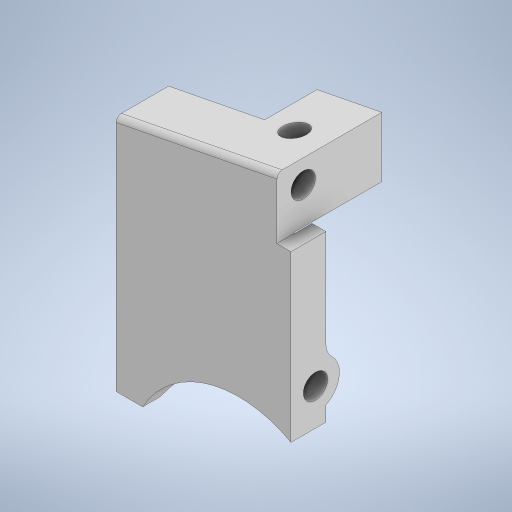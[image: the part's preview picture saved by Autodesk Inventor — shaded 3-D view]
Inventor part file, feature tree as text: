
AUTODESK INVENTOR PART (.ipt)
format: ipt  version: 2023.5 (Build 275446000, 446)  size: 538,112 bytes
history: native  units: mm
features: sketch x21, projected_geometry x19, extrude x17, reference x12, other x9, fillet x5, hole x4
ambient origin geometry x8: Origin, YZ Plane, XZ Plane, XY Plane, X Axis, Y Axis, Z Axis, Center Point
bodies: Body1 (feature_tree)
feature tree (87):
  other  "Bryła1"
  extrude  "Wyciągnięcie proste1"  Depth=2.0mm TaperAngle=0.0deg
  extrude  "Wyciągnięcie proste2"  Depth=5.0mm TaperAngle=0.0deg
  extrude  "Wyciągnięcie proste3"  Depth=4.0mm TaperAngle=0.0deg
  extrude  "Wyciągnięcie proste4"  Depth=6.0mm TaperAngle=0.0deg
  extrude  "Wyciągnięcie proste5"  Depth=1.0mm TaperAngle=0.0deg
  hole  "Otwór1"  [1 undecoded]
  extrude  "Wyciągnięcie proste6"  Depth=6.0mm
  hole  "Otwór2"  [1 undecoded]
  hole  "Otwór3"  [1 undecoded]
  extrude  "Wyciągnięcie proste7"  Depth=6.0mm
  extrude  "Wyciągnięcie proste8"  TaperAngle=0.0deg  [1 undecoded]
  fillet  "Zaokrąglenie1"  Radius=1.0mm
  extrude  "Wyciągnięcie proste9"  Depth=2.0mm TaperAngle=0.0deg
  extrude  "Wyciągnięcie proste10"  Depth=2.0mm
  extrude  "Wyciągnięcie proste11"  Depth=25.0mm
  extrude  "Wyciągnięcie proste12"  TaperAngle=0.0deg  [1 undecoded]
  extrude  "Wyciągnięcie proste13"  TaperAngle=0.0deg  [1 undecoded]
  fillet  "Zaokrąglenie2"  Radius=5.5mm
  hole  "Otwór4"  [1 undecoded]
  extrude  "Wyciągnięcie proste14"  Depth=2.0mm TaperAngle=0.0deg
  extrude  "Wyciągnięcie proste15"  Depth=2.0mm TaperAngle=0.0deg
  extrude  "Wyciągnięcie proste16"  Depth=2.0mm TaperAngle=0.0deg
  fillet  "Zaokrąglenie3"  Radius=2.0mm
  fillet  "Zaokrąglenie5"  Radius=1.0mm
  extrude  "Wyciągnięcie proste17"  Depth=2.0mm TaperAngle=0.0deg
  fillet  "Zaokrąglenie6"  [1 undecoded]
  sketch  "Szkic1"
  reference  "Odniesienie1"
  reference  "Odniesienie2"
  reference  "Odniesienie3"
  reference  "Odniesienie4"
  reference  "Odniesienie5"
  sketch  "Szkic2"
  reference  "Odniesienie6"
  projected_geometry  "Pętla rzutowana1"
  sketch  "Szkic3"
  reference  "Odniesienie7"
  reference  "Odniesienie8"
  projected_geometry  "Pętla rzutowana2"
  sketch  "Szkic4"
  projected_geometry  "Pętla rzutowana3"
  reference  "Odniesienie9"
  sketch  "Szkic5"
  projected_geometry  "Pętla rzutowana4"
  projected_geometry  "Pętla rzutowana5"
  sketch  "Szkic6"
  projected_geometry  "Pętla rzutowana6"
  sketch  "Szkic7"
  projected_geometry  "Pętla rzutowana7"
  sketch  "Szkic8"
  projected_geometry  "Pętla rzutowana8"
  sketch  "Szkic9"
  reference  "Odniesienie10"
  sketch  "Szkic10"
  projected_geometry  "Pętla rzutowana9"
  reference  "Odniesienie11"
  reference  "Odniesienie12"
  sketch  "Szkic11"
  projected_geometry  "Pętla rzutowana10"
  sketch  "Szkic12"
  sketch  "Szkic13"
  projected_geometry  "Pętla rzutowana11"
  projected_geometry  "Pętla rzutowana12"
  sketch  "Szkic14"
  projected_geometry  "Pętla rzutowana13"
  projected_geometry  "Pętla rzutowana14"
  sketch  "Szkic15"
  projected_geometry  "Pętla rzutowana15"
  sketch  "Szkic16"
  sketch  "Szkic17"
  sketch  "Szkic18"
  projected_geometry  "Pętla rzutowana16"
  sketch  "Szkic19"
  projected_geometry  "Pętla rzutowana17"
  sketch  "Szkic20"
  projected_geometry  "Pętla rzutowana18"
  sketch  "Szkic21"
  projected_geometry  "Pętla rzutowana19"
  parser-record x1  (decoder bookkeeping rows leaked as tree rows — omitted from the tree; the rows remain in map.json)
  other  "stratos_v2_mechanics.iam"
  other  "nozzyk:1"
  other  "podstawa_v2:1"
  other  "montaz_osi:1"
  other  "MikroSumo:1"
  other  "lipo-300:1"
  other  "pcb_dolne:1"
note: 8 required parameter values undecoded (feature->parameter linkage not recoverable at this tier; creation-order binding heuristic only, values carry confidence <= 0.55)
note: 1 file-system path scrubbed to <path> (originals preserved in map.json)
